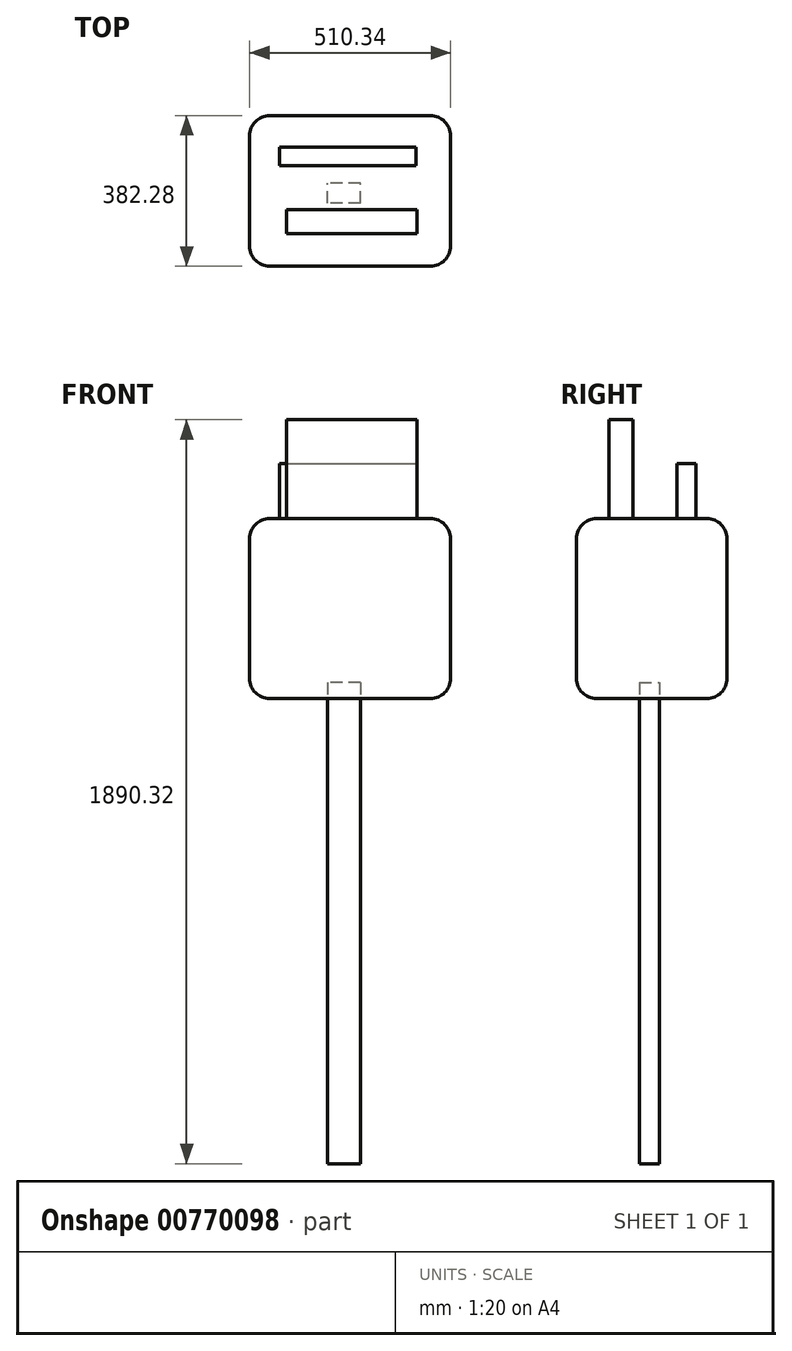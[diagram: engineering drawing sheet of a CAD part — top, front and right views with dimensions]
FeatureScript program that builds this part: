
annotation { "Feature Type Name" : "Feature", "Feature Type Description" : "" }
export const myFeature = defineFeature(function(context is Context, id is Id, definition is map)
    precondition{}
    {
        {
            var Q0;
            Q0=qCreatedBy(makeId("Top.planeOp"),FACE);
            var sketch = newSketch(context, id + "F0", { "sketchPlane" : qUnion([Q0])});
            skLineSegment(sketch, "E0.bottom", {"start": v(-576.6, 473.24) * mm, "end": v(-66.26, 473.24) * mm});
            skLineSegment(sketch, "E0.top", {"start": v(-576.6, 90.96) * mm, "end": v(-66.26, 90.96) * mm});
            skLineSegment(sketch, "E0.left", {"start": v(-576.6, 473.24) * mm, "end": v(-576.6, 90.96) * mm});
            skLineSegment(sketch, "E0.right", {"start": v(-66.26, 473.24) * mm, "end": v(-66.26, 90.96) * mm});
            skSolve(sketch);
        }
        {
            var Q0;
            Q0=makeQuery(id+"F0.imprint","IMPRINT",FACE,{"disambiguationData":[TD([[makeQuery(id+"F0.imprint","IMPRINT",EDGE,{"derivedFrom":sQuery(id+"F0.wireOp",EDGE,"E0.bottom")}),-1.0]])]});
            extrude(context, id + "F1", {"entities" : qUnion([Q0]), "depth" : 457.2 * mm, "offsetDistance" : 25.4 * mm});
        }
        {
            var Q0;
            Q0=makeQuery(id+"F1.opExtrude","CAP_FACE",FACE,{"disambiguationData":[OSD([sQuery(id+"F0.wireOp",EDGE,"E0.bottom"),sQuery(id+"F0.wireOp",EDGE,"E0.top"),sQuery(id+"F0.wireOp",EDGE,"E0.left"),sQuery(id+"F0.wireOp",EDGE,"E0.right")])],"isStart":false});
            var Q1;
            Q1=makeQuery(id+"F1.opExtrude","SWEPT_FACE",FACE,{"disambiguationData":[OSD([sQuery(id+"F0.wireOp",EDGE,"E0.bottom")])]});
            var Q2;
            Q2=makeQuery(id+"F1.opExtrude","SWEPT_FACE",FACE,{"disambiguationData":[OSD([sQuery(id+"F0.wireOp",EDGE,"E0.left")])]});
            var Q3;
            Q3=makeQuery(id+"F1.opExtrude","SWEPT_FACE",FACE,{"disambiguationData":[OSD([sQuery(id+"F0.wireOp",EDGE,"E0.top")])]});
            var Q4;
            Q4=makeQuery(id+"F1.opExtrude","SWEPT_FACE",FACE,{"disambiguationData":[OSD([sQuery(id+"F0.wireOp",EDGE,"E0.right")])]});
            fillet(context, id + "F2", {"entities" : qUnion([Q0, Q1, Q2, Q3, Q4]), "radius" : 50.8 * mm, "tangentPropagation" : true, "allowEdgeOverflow" : false});
        }
        {
            var Q0;
            Q0=makeQuery(id+"F1.opExtrude","SWEPT_FACE",FACE,{"disambiguationData":[OSD([sQuery(id+"F0.wireOp",EDGE,"E0.left")])]});
            extrude(context, id + "F3", {"entities" : qUnion([Q0]), "operationType" : NewBodyOperationType.ADD, "depth" : -50.8 * mm, "offsetDistance" : 25.4 * mm});
        }
        {
            var Q0;
            Q0=makeQuery(id+"F1.opExtrude","SWEPT_FACE",FACE,{"disambiguationData":[OSD([sQuery(id+"F0.wireOp",EDGE,"E0.right")])]});
            extrude(context, id + "F4", {"entities" : qUnion([Q0]), "operationType" : NewBodyOperationType.ADD, "oppositeDirection" : true, "depth" : 50.8 * mm, "offsetDistance" : 25.4 * mm});
        }
        {
            var Q0;
            Q0=qCreatedBy(makeId("Front.planeOp"),FACE);
            var sketch = newSketch(context, id + "F5", { "sketchPlane" : qUnion([Q0])});
            skLineSegment(sketch, "E1.bottom", {"start": v(-208.53, -86.04) * mm, "end": v(-292.06, -86.04) * mm});
            skLineSegment(sketch, "E1.top", {"start": v(-208.53, -1308.66) * mm, "end": v(-292.06, -1308.66) * mm});
            skLineSegment(sketch, "E1.left", {"start": v(-208.53, -86.04) * mm, "end": v(-208.53, -1308.66) * mm});
            skLineSegment(sketch, "E1.right", {"start": v(-292.06, -86.04) * mm, "end": v(-292.06, -1308.66) * mm});
            skSolve(sketch);
        }
        {
            var Q0;
            Q0 = qSketchRegion(id + "F5", true);
            extrude(context, id + "F6", {"entities" : qUnion([Q0]), "depth" : 50.8 * mm, "offsetDistance" : 25.4 * mm});
        }
        {
            var Q0;
            Q0=makeQuery(id+"F6.opExtrude","SWEPT_BODY",BODY,{"disambiguationData":[OSD([sQuery(id+"F5.wireOp",EDGE,"E1.bottom"),sQuery(id+"F5.wireOp",EDGE,"E1.top"),sQuery(id+"F5.wireOp",EDGE,"E1.left"),sQuery(id+"F5.wireOp",EDGE,"E1.right")])]});
            var Q1;
            Q1=makeQuery(id+"F6.opExtrude","CAP_FACE",FACE,{"disambiguationData":[OSD([sQuery(id+"F5.wireOp",EDGE,"E1.bottom"),sQuery(id+"F5.wireOp",EDGE,"E1.top"),sQuery(id+"F5.wireOp",EDGE,"E1.left"),sQuery(id+"F5.wireOp",EDGE,"E1.right")])],"isStart":false});
            transform(context, id + "F7", {"entities" : qUnion([Q0]), "transformType" : TransformType.TRANSLATION_DISTANCE, "transformDirection" : qUnion([Q1]), "distance" : 330.2 * mm, "oppositeDirection" : true, "makeCopy" : false});
        }
        {
            var Q0;
            Q0=makeQuery(id+"F6.opExtrude","SWEPT_BODY",BODY,{"disambiguationData":[OSD([sQuery(id+"F5.wireOp",EDGE,"E1.bottom"),sQuery(id+"F5.wireOp",EDGE,"E1.top"),sQuery(id+"F5.wireOp",EDGE,"E1.left"),sQuery(id+"F5.wireOp",EDGE,"E1.right")])]});
            transform(context, id + "F8", {"entities" : qUnion([Q0]), "transformType" : TransformType.TRANSLATION_3D, "dx" : -86.36 * mm, "dy" : -27.94 * mm, "dz" : 127 * mm, "makeCopy" : false});
        }
        {
            var Q0;
            Q0=makeQuery(id+"F1.opExtrude","CAP_FACE",FACE,{"disambiguationData":[OSD([sQuery(id+"F0.wireOp",EDGE,"E0.bottom"),sQuery(id+"F0.wireOp",EDGE,"E0.top"),sQuery(id+"F0.wireOp",EDGE,"E0.left"),sQuery(id+"F0.wireOp",EDGE,"E0.right")])],"isStart":false});
            var sketch = newSketch(context, id + "F9", { "sketchPlane" : qUnion([Q0])});
            skLineSegment(sketch, "E2.bottom", {"start": v(-501.27, 393.85) * mm, "end": v(-154.4, 393.85) * mm});
            skLineSegment(sketch, "E2.top", {"start": v(-501.27, 346.21) * mm, "end": v(-154.4, 346.21) * mm});
            skLineSegment(sketch, "E2.left", {"start": v(-501.27, 393.85) * mm, "end": v(-501.27, 346.21) * mm});
            skLineSegment(sketch, "E2.right", {"start": v(-154.4, 393.85) * mm, "end": v(-154.4, 346.21) * mm});
            skSolve(sketch);
        }
        {
            var Q0;
            Q0=makeQuery(id+"F9.imprint","IMPRINT",FACE,{"disambiguationData":[TD([[makeQuery(id+"F9.imprint","IMPRINT",EDGE,{"derivedFrom":sQuery(id+"F9.wireOp",EDGE,"E2.bottom")}),-1.0]])]});
            extrude(context, id + "F10", {"entities" : qUnion([Q0]), "operationType" : NewBodyOperationType.ADD, "depth" : 139.7 * mm, "offsetDistance" : 25.4 * mm});
        }
        {
            var Q0;
            Q0=makeQuery(id+"F1.opExtrude","SWEPT_BODY",BODY,{"disambiguationData":[OSD([sQuery(id+"F0.wireOp",EDGE,"E0.bottom"),sQuery(id+"F0.wireOp",EDGE,"E0.top"),sQuery(id+"F0.wireOp",EDGE,"E0.left"),sQuery(id+"F0.wireOp",EDGE,"E0.right")])]});
            transform(context, id + "F11", {"entities" : qUnion([Q0]), "transformType" : TransformType.COPY});
        }
        {
            var Q0;
            Q0=makeQuery(id+"F1.opExtrude","CAP_FACE",FACE,{"disambiguationData":[OSD([sQuery(id+"F0.wireOp",EDGE,"E0.bottom"),sQuery(id+"F0.wireOp",EDGE,"E0.top"),sQuery(id+"F0.wireOp",EDGE,"E0.left"),sQuery(id+"F0.wireOp",EDGE,"E0.right")])],"isStart":false});
            var sketch = newSketch(context, id + "F12", { "sketchPlane" : qUnion([Q0])});
            skLineSegment(sketch, "E3.bottom", {"start": v(-482.7, 234.45) * mm, "end": v(-151.87, 234.45) * mm});
            skLineSegment(sketch, "E3.top", {"start": v(-482.7, 173.91) * mm, "end": v(-151.87, 173.91) * mm});
            skLineSegment(sketch, "E3.left", {"start": v(-482.7, 234.45) * mm, "end": v(-482.7, 173.91) * mm});
            skLineSegment(sketch, "E3.right", {"start": v(-151.87, 234.45) * mm, "end": v(-151.87, 173.91) * mm});
            skSolve(sketch);
        }
        {
            var Q0;
            Q0=makeQuery(id+"F12.imprint","IMPRINT",FACE,{"disambiguationData":[TD([[makeQuery(id+"F12.imprint","IMPRINT",EDGE,{"derivedFrom":sQuery(id+"F12.wireOp",EDGE,"E3.bottom")}),-1.0]])]});
            extrude(context, id + "F13", {"entities" : qUnion([Q0]), "depth" : 251.46 * mm, "offsetDistance" : 25.4 * mm});
        }
    });
